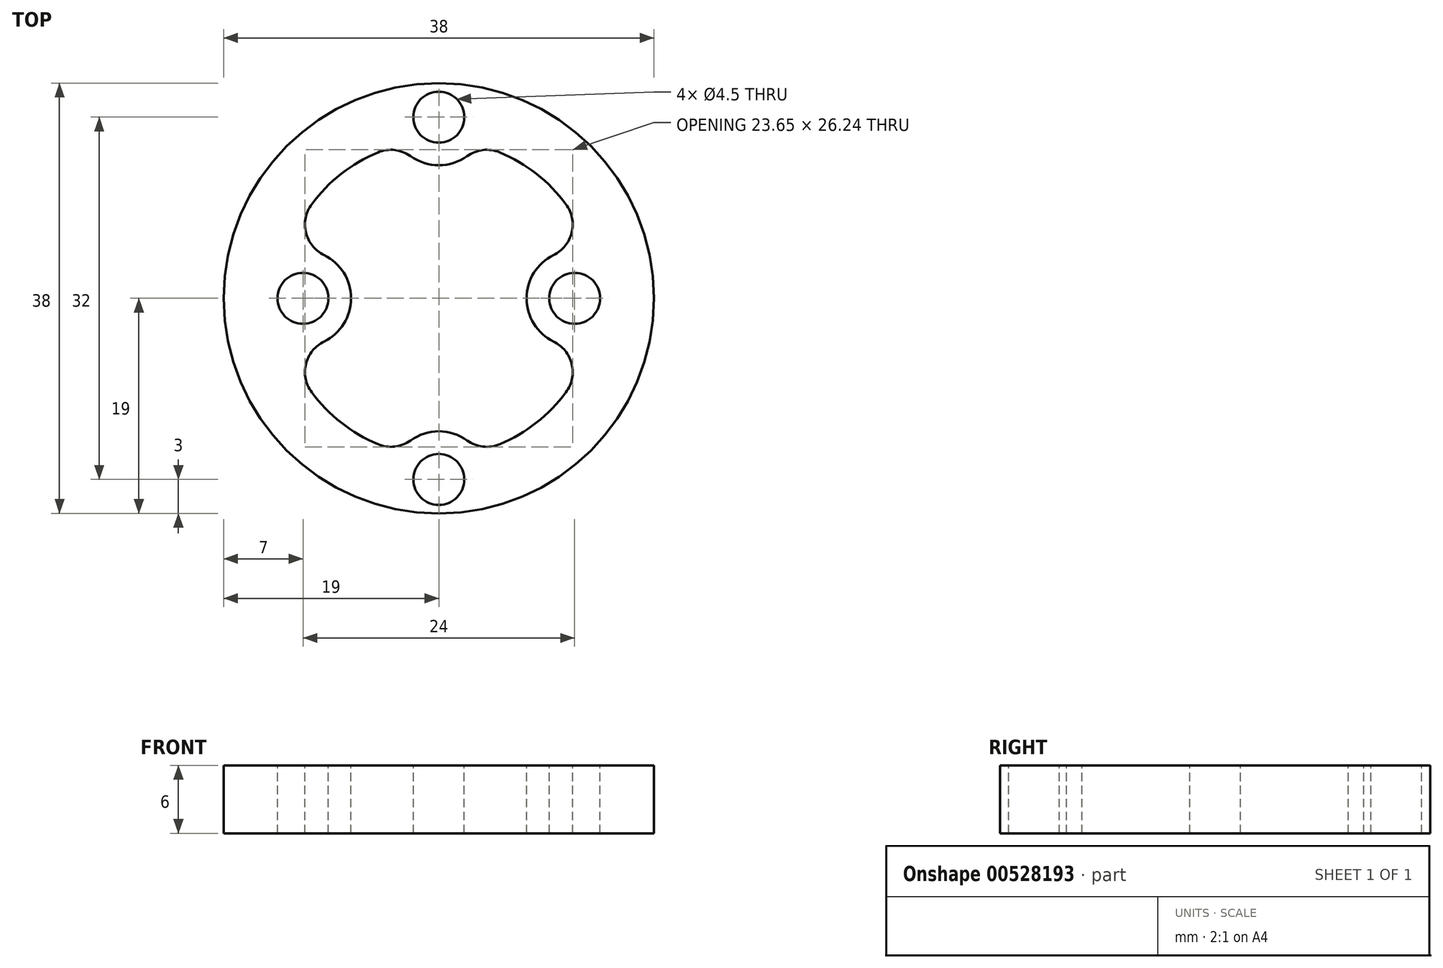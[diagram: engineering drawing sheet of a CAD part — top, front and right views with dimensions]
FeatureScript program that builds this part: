
annotation { "Feature Type Name" : "Feature", "Feature Type Description" : "" }
export const myFeature = defineFeature(function(context is Context, id is Id, definition is map)
    precondition{}
    {
        {
            var Q0;
            Q0=qCreatedBy(makeId("Top.planeOp"),FACE);
            var sketch = newSketch(context, id + "F0", { "sketchPlane" : qUnion([Q0])});
            skCircle(sketch, "E0", {"center": v(-65, 34.5) * mm, "radius": 19 * mm});
            skCircle(sketch, "E1", {"center": v(-65, 50.5) * mm, "radius": 2.25 * mm});
            skCircle(sketch, "E2", {"center": v(-65, 18.5) * mm, "radius": 2.25 * mm});
            skCircle(sketch, "E3", {"center": v(-53, 34.5) * mm, "radius": 2.25 * mm});
            skCircle(sketch, "E4", {"center": v(-77, 34.5) * mm, "radius": 2.25 * mm});
            skArc(sketch, "E5", {"start": v(-78.38, 30.48) * mm, "mid": v(-72.75, 34.5) * mm, "end": v(-78.38, 38.52) * mm});
            skArc(sketch, "E6", {"start": v(-68.46, 48.03) * mm, "mid": v(-65, 46.25) * mm, "end": v(-61.54, 48.03) * mm});
            skArc(sketch, "E7", {"start": v(-51.62, 38.52) * mm, "mid": v(-57.25, 34.5) * mm, "end": v(-51.62, 30.48) * mm});
            skArc(sketch, "E8", {"start": v(-61.54, 20.97) * mm, "mid": v(-65, 22.75) * mm, "end": v(-68.46, 20.97) * mm});
            skArc(sketch, "E9.trimOffspring", {"start": v(-68.46, 48.03) * mm, "mid": v(-74.67, 44.58) * mm, "end": v(-78.38, 38.52) * mm});
            skArc(sketch, "E10.trimOffspring", {"start": v(-51.62, 38.52) * mm, "mid": v(-55.33, 44.58) * mm, "end": v(-61.54, 48.03) * mm});
            skArc(sketch, "E11.trimOffspring", {"start": v(-61.54, 20.97) * mm, "mid": v(-55.33, 24.42) * mm, "end": v(-51.62, 30.48) * mm});
            skArc(sketch, "E12.trimOffspring", {"start": v(-78.38, 30.48) * mm, "mid": v(-74.67, 24.42) * mm, "end": v(-68.46, 20.97) * mm});
            skSolve(sketch);
        }
        {
            var Q0;
            Q0=makeQuery(id+"F0.imprint","IMPRINT",FACE,{"disambiguationData":[TD([[makeQuery(id+"F0.imprint","IMPRINT",EDGE,{"derivedFrom":sQuery(id+"F0.wireOp",EDGE,"E0")}),1.0]])]});
            extrude(context, id + "F1", {"entities" : qUnion([Q0]), "oppositeDirection" : true, "depth" : 6 * mm, "offsetDistance" : 25.4 * mm});
        }
        {
            var Q0;
            Q0=makeQuery(id+"F1.opExtrude","SWEPT_EDGE",EDGE,{"disambiguationData":[OSD([sQuery(id+"F0.wireOp",EDGE,"E8"),sQuery(id+"F0.wireOp",EDGE,"E11.trimOffspring")])]});
            var Q1;
            Q1=makeQuery(id+"F1.opExtrude","SWEPT_EDGE",EDGE,{"disambiguationData":[OSD([sQuery(id+"F0.wireOp",EDGE,"E8"),sQuery(id+"F0.wireOp",EDGE,"E12.trimOffspring")])]});
            var Q2;
            Q2=makeQuery(id+"F1.opExtrude","SWEPT_EDGE",EDGE,{"disambiguationData":[OSD([sQuery(id+"F0.wireOp",EDGE,"E5"),sQuery(id+"F0.wireOp",EDGE,"E12.trimOffspring")])]});
            var Q3;
            Q3=makeQuery(id+"F1.opExtrude","SWEPT_EDGE",EDGE,{"disambiguationData":[OSD([sQuery(id+"F0.wireOp",EDGE,"E5"),sQuery(id+"F0.wireOp",EDGE,"E9.trimOffspring")])]});
            var Q4;
            Q4=makeQuery(id+"F1.opExtrude","SWEPT_EDGE",EDGE,{"disambiguationData":[OSD([sQuery(id+"F0.wireOp",EDGE,"E7"),sQuery(id+"F0.wireOp",EDGE,"E11.trimOffspring")])]});
            var Q5;
            Q5=makeQuery(id+"F1.opExtrude","SWEPT_EDGE",EDGE,{"disambiguationData":[OSD([sQuery(id+"F0.wireOp",EDGE,"E6"),sQuery(id+"F0.wireOp",EDGE,"E9.trimOffspring")])]});
            var Q6;
            Q6=makeQuery(id+"F1.opExtrude","SWEPT_EDGE",EDGE,{"disambiguationData":[OSD([sQuery(id+"F0.wireOp",EDGE,"E6"),sQuery(id+"F0.wireOp",EDGE,"E10.trimOffspring")])]});
            var Q7;
            Q7=makeQuery(id+"F1.opExtrude","SWEPT_EDGE",EDGE,{"disambiguationData":[OSD([sQuery(id+"F0.wireOp",EDGE,"E7"),sQuery(id+"F0.wireOp",EDGE,"E10.trimOffspring")])]});
            fillet(context, id + "F2", {"entities" : qUnion([Q0, Q1, Q2, Q3, Q4, Q5, Q6, Q7]), "radius" : 3 * mm, "tangentPropagation" : true, "allowEdgeOverflow" : false});
        }
    });
